# Revit family: Screens-Teknion-JNSESL_Solid_Elevated_Leg_Mounted-R2018
name_source: partatom
category: Furniture
revit_build: Autodesk Revit 2018 (Build: 20190510_1515(x64)
units: mm (PartAtom-declared; Revit-internal decimal feet)

## family parameters
Always vertical = Yes
Cut with Voids When Loaded = No
OmniClass Number = 23.40.20.00
OmniClass Title = General Furniture and Specialties
Room Calculation Point = No
Shared = Yes
Work Plane-Based = No

## types (3) — shared parameters
Assembly Code = E2020200
Manufacturer = Teknion
Manufacturer Fax = 416.661.4586
Part Number = JNSESL
Product Documentation Link = https://www.teknion.com
Product Line = Expansion Cityline
Product Page URL = https://www.teknion.com
Series = Expansion Cityline
Sustainability Data = https://www.teknion.com
URL = www.teknion.com
Unit Weight URL = http://www.teknion.com
Warranty = http://www.teknion.com

## per-type parameters (varying)
| type | Description | Model |
| Left Configuration | Solid Elevated Screen – Leg-Mounted, Left Configuration, 10" from Floor Modesty Base Height, Standard Corner Detail | JNSESLL10_____S_ |
| Right Configuration | Solid Elevated Screen – Leg-Mounted, Right Configuration, 10" from Floor Modesty Base Height, Standard Corner Detail | JNSESLR10_____S_ |
| Double-Sided Leg Overlay | Solid Elevated Screen – Leg-Mounted, Double-Sided Leg Overlay Configuration, 10" from Floor Modesty Base Height, Standard Corner Detail | JNSESLD10_____S_ |

type visibility flags: 3 boolean params named "<type name>" — each type sets only its own to Yes (folded from table)

## geometry (parser evidence)
native form markers: Sweep x2
no freeform markers — native parametric forms only
